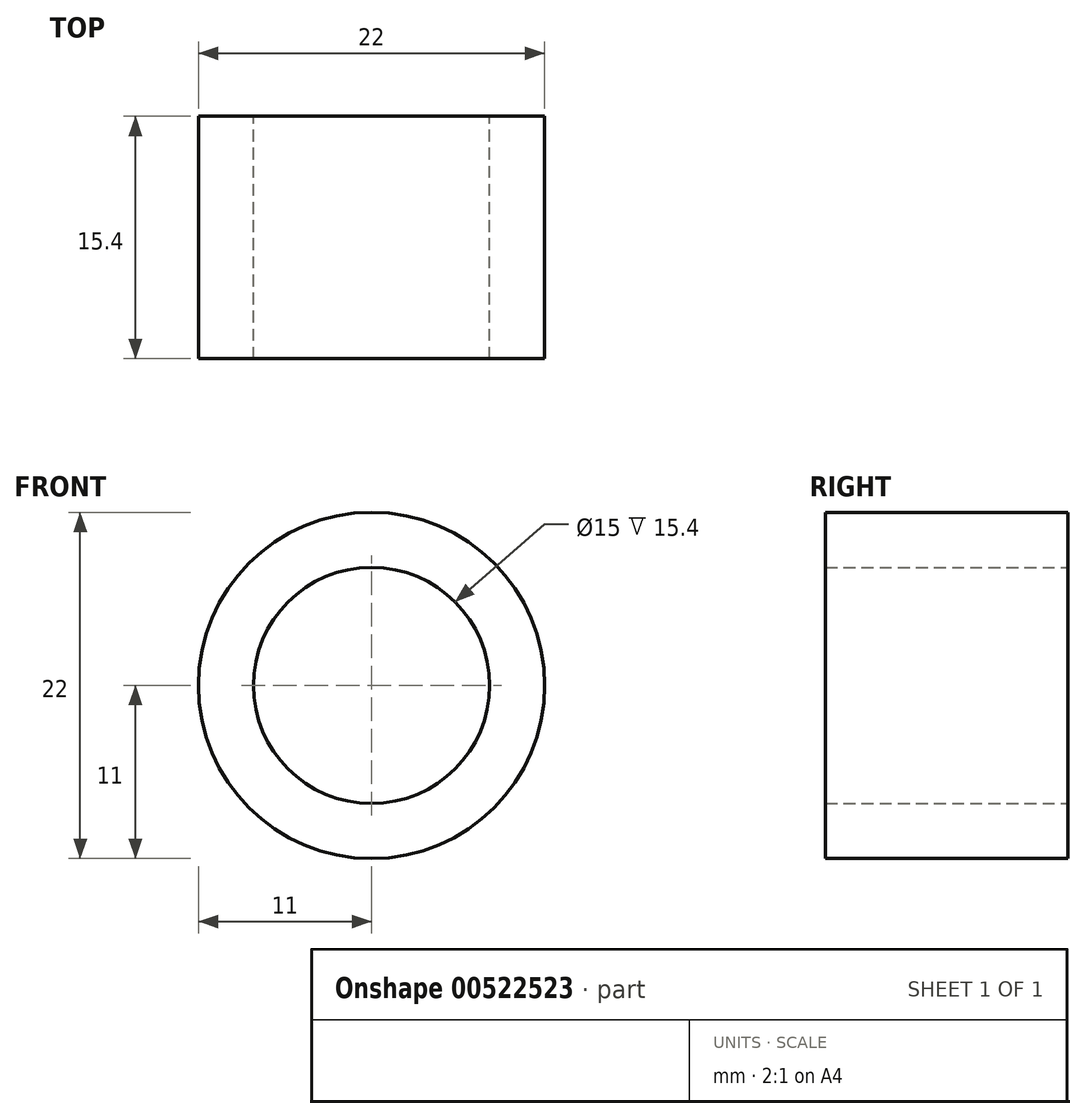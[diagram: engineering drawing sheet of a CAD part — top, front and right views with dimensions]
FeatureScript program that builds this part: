
annotation { "Feature Type Name" : "Feature", "Feature Type Description" : "" }
export const myFeature = defineFeature(function(context is Context, id is Id, definition is map)
    precondition{}
    {
        {
            var Q0;
            Q0=qCreatedBy(makeId("Front.planeOp"),FACE);
            var sketch = newSketch(context, id + "F0", { "sketchPlane" : qUnion([Q0])});
            skCircle(sketch, "E0", {"center": v(0, 0) * mm, "radius": 7.5 * mm});
            skCircle(sketch, "E1", {"center": v(0, 0) * mm, "radius": 11 * mm});
            skSolve(sketch);
        }
        {
            var Q0;
            Q0=makeQuery(id+"F0.imprint","IMPRINT",FACE,{"disambiguationData":[TD([[makeQuery(id+"F0.imprint","IMPRINT",EDGE,{"derivedFrom":sQuery(id+"F0.wireOp",EDGE,"E0")}),-1.0]])]});
            extrude(context, id + "F1", {"entities" : qUnion([Q0]), "depth" : 15.4 * mm});
        }
    });
